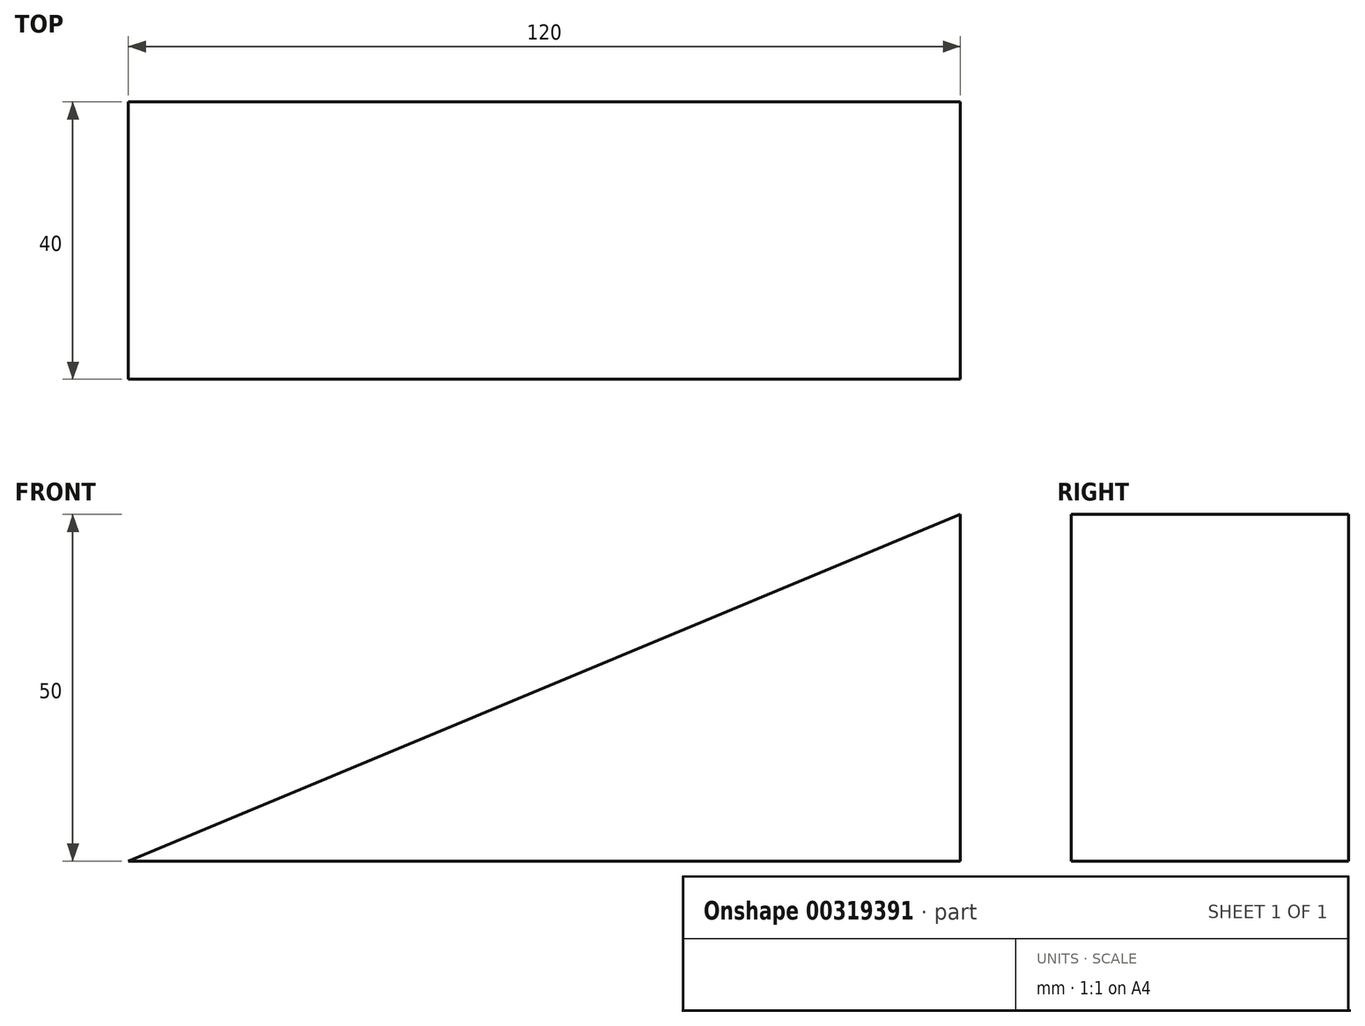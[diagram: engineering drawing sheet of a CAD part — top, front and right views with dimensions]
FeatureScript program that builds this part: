
annotation { "Feature Type Name" : "Feature", "Feature Type Description" : "" }
export const myFeature = defineFeature(function(context is Context, id is Id, definition is map)
    precondition{}
    {
        {
            var Q0;
            Q0=qCreatedBy(makeId("Top.planeOp"),FACE);
            var sketch = newSketch(context, id + "F0", { "sketchPlane" : qUnion([Q0])});
            skLineSegment(sketch, "E0.bottom", {"start": v(-59.88, 47.41) * mm, "end": v(60.12, 47.41) * mm});
            skLineSegment(sketch, "E0.top", {"start": v(-59.88, 7.41) * mm, "end": v(60.12, 7.41) * mm});
            skLineSegment(sketch, "E0.left", {"start": v(-59.88, 47.41) * mm, "end": v(-59.88, 7.41) * mm});
            skLineSegment(sketch, "E0.right", {"start": v(60.12, 47.41) * mm, "end": v(60.12, 7.41) * mm});
            skSolve(sketch);
        }
        {
            var Q0;
            Q0=makeQuery(id+"F0.imprint","IMPRINT",FACE,{"disambiguationData":[TD([[makeQuery(id+"F0.imprint","IMPRINT",EDGE,{"derivedFrom":sQuery(id+"F0.wireOp",EDGE,"E0.bottom")}),-1.0]])]});
            extrude(context, id + "F1", {"entities" : qUnion([Q0]), "depth" : 50 * mm});
        }
        {
            var Q0;
            Q0=makeQuery(id+"F1.opExtrude","SWEPT_FACE",FACE,{"disambiguationData":[OSD([sQuery(id+"F0.wireOp",EDGE,"E0.top")])]});
            var sketch = newSketch(context, id + "F2", { "sketchPlane" : qUnion([Q0])});
            skLineSegment(sketch, "E1", {"start": v(-59.88, 0) * mm, "end": v(-59.88, 50) * mm});
            skLineSegment(sketch, "E2", {"start": v(-59.88, 50) * mm, "end": v(60.12, 50) * mm});
            skLineSegment(sketch, "E3", {"start": v(60.12, 50) * mm, "end": v(-59.88, 0) * mm});
            skSolve(sketch);
        }
        {
            var Q0;
            Q0=makeQuery(id+"F2.imprint","IMPRINT",FACE,{"disambiguationData":[TD([[makeQuery(id+"F2.imprint","IMPRINT",EDGE,{"derivedFrom":sQuery(id+"F2.wireOp",EDGE,"E1")}),1.0]])]});
            extrude(context, id + "F3", {"entities" : qUnion([Q0]), "operationType" : NewBodyOperationType.REMOVE, "endBound" : BoundingType.THROUGH_ALL, "oppositeDirection" : true, "depth" : 25 * mm});
        }
    });
